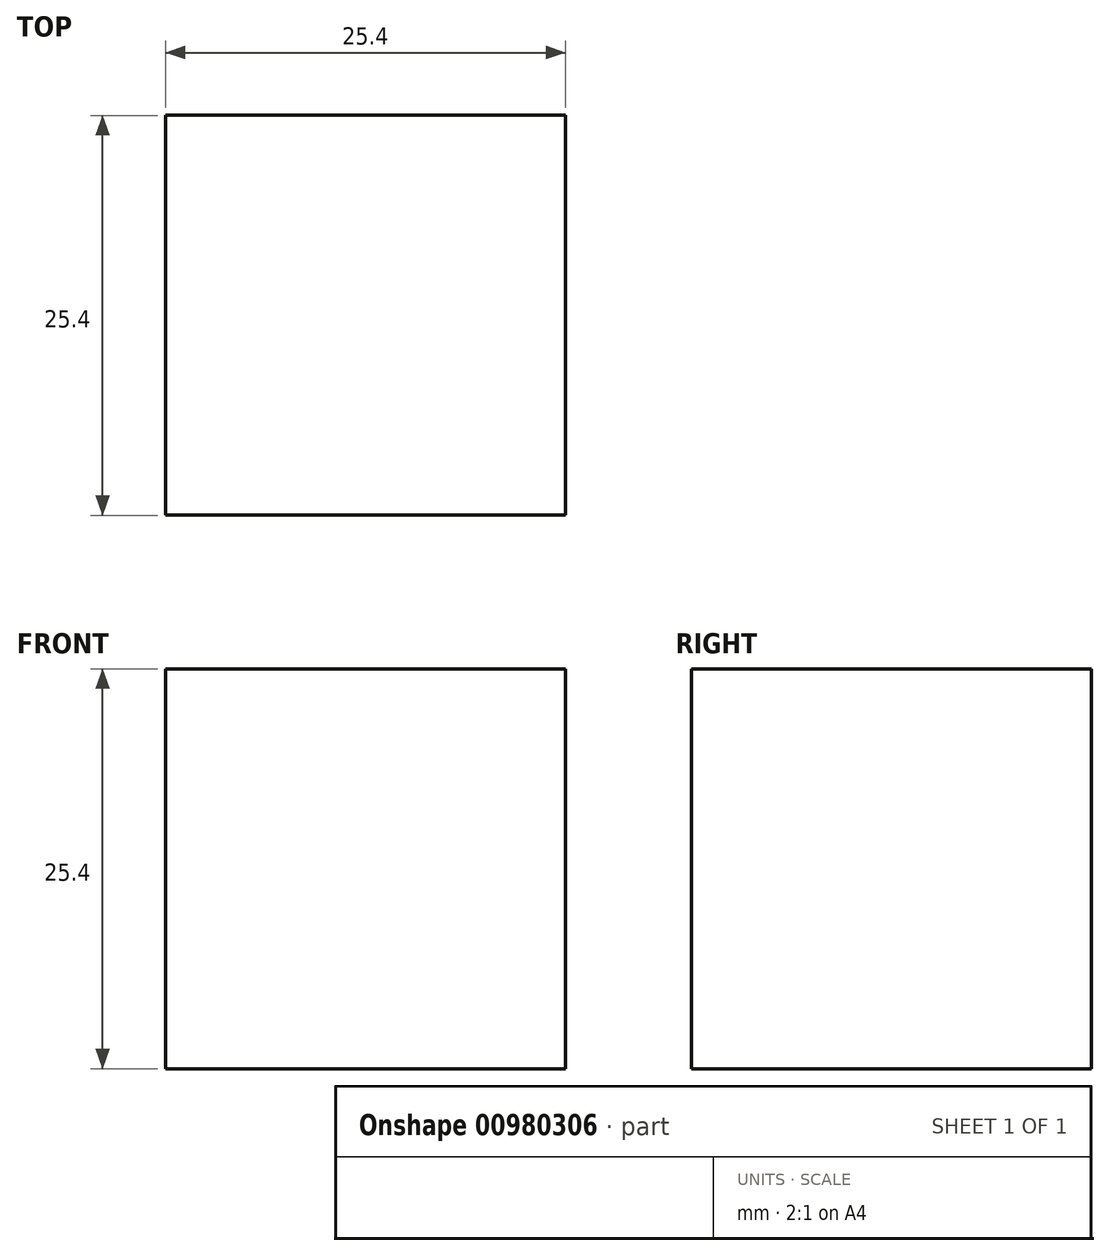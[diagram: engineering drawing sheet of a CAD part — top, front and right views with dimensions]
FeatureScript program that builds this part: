
annotation { "Feature Type Name" : "Feature", "Feature Type Description" : "" }
export const myFeature = defineFeature(function(context is Context, id is Id, definition is map)
    precondition{}
    {
        {
            var Q0;
            Q0=qCreatedBy(makeId("Top.planeOp"),FACE);
            var sketch = newSketch(context, id + "F0", { "sketchPlane" : qUnion([Q0])});
            skLineSegment(sketch, "E0.bottom", {"start": v(-16.87, 10.52) * mm, "end": v(8.53, 10.52) * mm});
            skLineSegment(sketch, "E0.top", {"start": v(-16.87, -14.88) * mm, "end": v(8.53, -14.88) * mm});
            skLineSegment(sketch, "E0.left", {"start": v(-16.87, 10.52) * mm, "end": v(-16.87, -14.88) * mm});
            skLineSegment(sketch, "E0.right", {"start": v(8.53, 10.52) * mm, "end": v(8.53, -14.88) * mm});
            skSolve(sketch);
        }
        {
            var Q0;
            Q0 = qSketchRegion(id + "F0", true);
            extrude(context, id + "F1", {"entities" : qUnion([Q0]), "depth" : 25.4 * mm, "offsetDistance" : 25.4 * mm});
        }
    });
